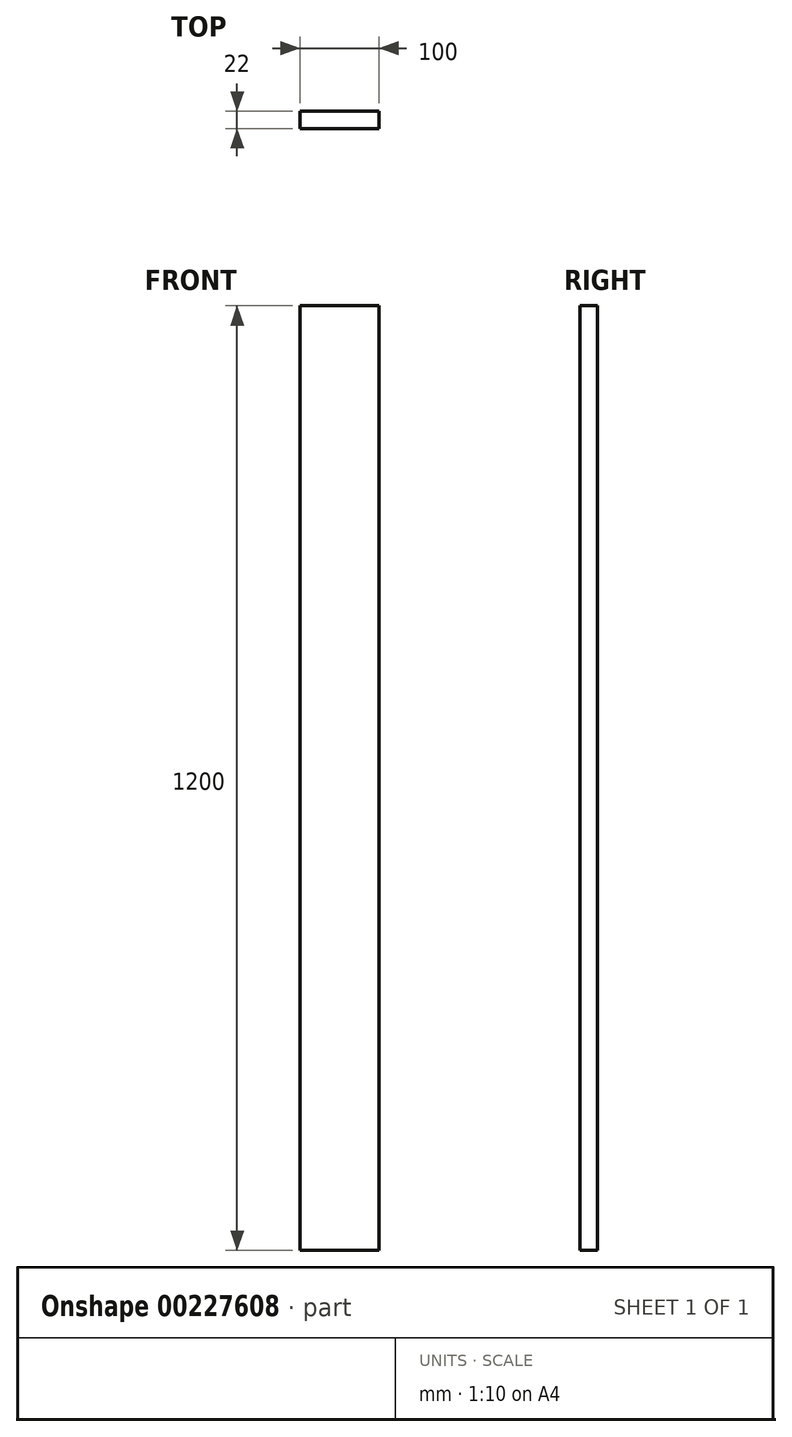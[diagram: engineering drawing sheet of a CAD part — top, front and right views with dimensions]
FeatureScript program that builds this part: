
annotation { "Feature Type Name" : "Feature", "Feature Type Description" : "" }
export const myFeature = defineFeature(function(context is Context, id is Id, definition is map)
    precondition{}
    {
        {
            var Q0;
            Q0=qCreatedBy(makeId("Front.planeOp"),FACE);
            var sketch = newSketch(context, id + "F0", { "sketchPlane" : qUnion([Q0])});
            skLineSegment(sketch, "E0.bottom", {"start": v(50, 600) * mm, "end": v(-50, 600) * mm});
            skLineSegment(sketch, "E0.top", {"start": v(50, -600) * mm, "end": v(-50, -600) * mm});
            skLineSegment(sketch, "E0.left", {"start": v(50, 600) * mm, "end": v(50, -600) * mm});
            skLineSegment(sketch, "E0.right", {"start": v(-50, 600) * mm, "end": v(-50, -600) * mm});
            skPoint(sketch, "E0.middle", {"position": v(0, 0) * mm});
            skSolve(sketch);
        }
        {
            var Q0;
            Q0 = qSketchRegion(id + "F0", true);
            extrude(context, id + "F1", {"entities" : qUnion([Q0]), "depth" : 22 * mm});
        }
    });
